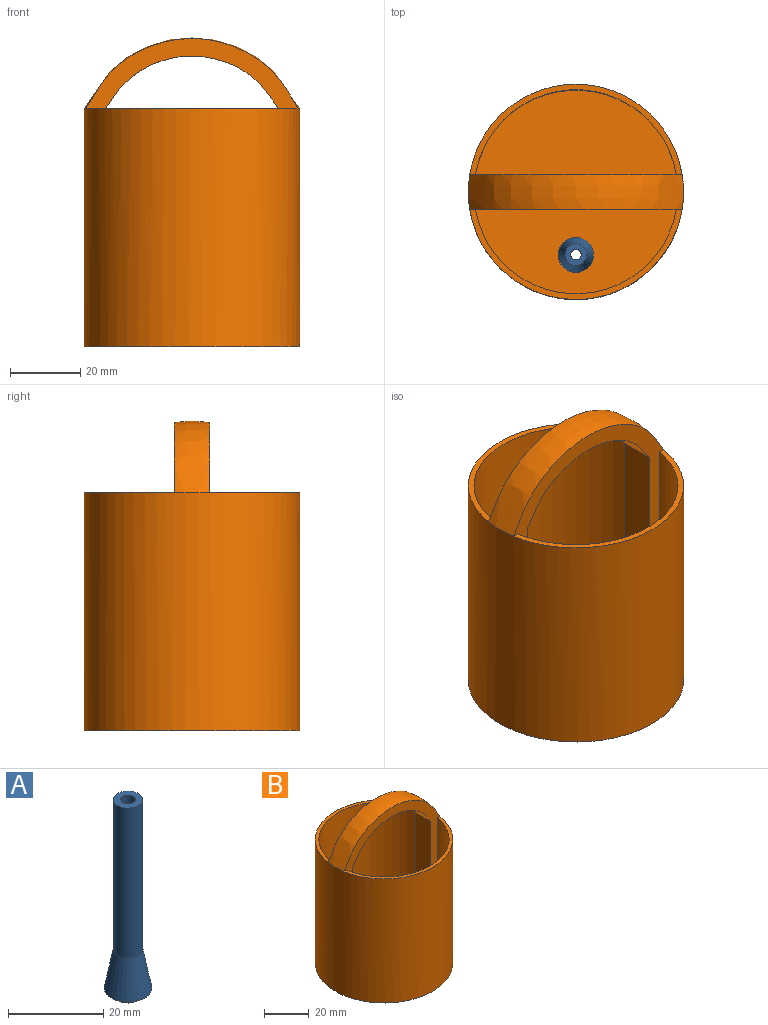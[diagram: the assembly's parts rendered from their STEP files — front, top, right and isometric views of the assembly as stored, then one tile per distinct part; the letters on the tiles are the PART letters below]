
ASSEMBLY  parts=2 mates=1
PART A: 7 faces, bbox 10x10x50 mm
  f0: plane 10x10mm, normal (0,0,-1), area 48.3mm2, adj f1,f2
  f1: cone r=5mm half-angle=10.8deg, axis (0,0,-1), area 259mm2, adj f0,f4
  f2: cylinder r=3.1mm len=6.2mm, axis (0,0,1), area 31.2mm2, adj f0,f3
  f3: plane 6.2x6.2mm, normal (0,0,-1), area 23.1mm2, adj f2,f6
  f4: cylinder r=3.1mm len=38.4mm, axis (0,0,-1), area 748mm2, adj f1,f5
  f5: plane 6.2x6.2mm, normal (0,0,1), area 23.1mm2, adj f4,f6
  f6: cylinder r=1.5mm len=50mm, axis (0,0,1), area 471.2mm2, adj f3,f5
PART B: 14 faces, bbox 61.6x61.3x89.1 mm
  f0: plane 60.49x25.66mm, normal (0,0,1), area 133.7mm2, adj f4,f9,f10
  f1: plane 60.49x25.66mm, normal (0,0,1), area 133.7mm2, adj f4,f6,f7
  f2: plane 58x57.13mm, normal (0,0,1), area 2526.1mm2, adj f3,f6,f7,f8,f9,f10,f11
  f3: cylinder r=3.1mm len=6.2mm, axis (0,0,1), area 31.2mm2, adj f2,f5
  f4: cylinder r=30.6mm len=67.6mm, axis (0,0,1), area 12997.1mm2, adj f0,f1,f5,f12
  f5: plane 61.2x61.2mm, normal (0,0,-1), area 2911.5mm2, adj f3,f4
  f6: cylinder r=29mm len=66mm, axis (0,0,-1), area 5349.7mm2, adj f1,f2,f7
  f7: plane 86.14x60.51mm, normal (0,-1,0), area 853.5mm2, adj f1,f2,f6,f8,f11,f12,f13
  f8: plane 66x10mm, normal (1,0,0), area 660mm2, adj f2,f7,f9,f13
  f9: plane 86.14x60.51mm, normal (0,1,0), area 853.5mm2, adj f0,f2,f8,f10,f11,f12,f13
  f10: cylinder r=29mm len=66mm, axis (0,0,-1), area 5349.7mm2, adj f0,f2,f9
  f11: plane 66x10mm, normal (-1,0,0), area 660mm2, adj f2,f7,f9,f13
  f12: bspline ~61.47x21.36mm, area 777.3mm2, adj f4,f7,f9
  f13: bspline ~49.13x15.63mm, area 605.1mm2, adj f7,f8,f9,f11
PLACE A t=(-59.8,-17.87,-23.73)mm
PLACE B t=(-59.8,-0.03,-23.73)mm
MATE fastened B.f3 <-> A.f6  axis (0,0,-1) through (-59.8,-17.87,-25.33)mm
